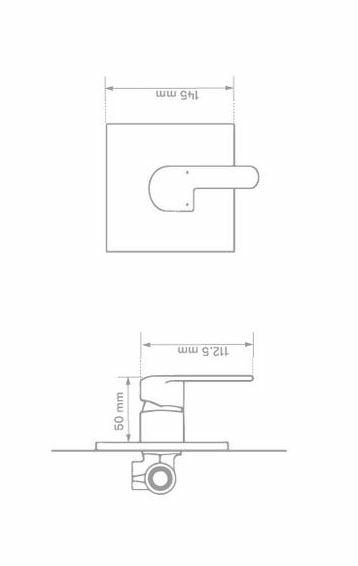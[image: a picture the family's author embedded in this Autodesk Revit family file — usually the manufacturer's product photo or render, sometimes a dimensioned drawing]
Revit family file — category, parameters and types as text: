
# Revit family: 01-1333-11 REGISTRO DUCHA ATLANTICO
name_source: partatom
category: Plumbing Fixtures
revit_build: Autodesk Revit 2018 (Build: 20170223_1515(x64)
units: mm (PartAtom-declared; Revit-internal decimal feet)

## family parameters
Cut with Voids When Loaded = No
Host = Face
OmniClass Number = 23.31.11.00
Part Type = Normal
Room Calculation Point = No
Round Connector Dimension = Use Diameter
Shared = No

## types (1)
- 01-1333-11
    Alto = 85 mm
    Ancho manija = 66 mm
    CW Connection = Yes
    Default Elevation = 0 mm  [stored 0 ft]
    Description = Registro
    Dim escudo = 60 mm
    HW Connection = Yes
    Link Ficha Tecnica = http://infotecnica.gricol.com
    Manufacturer = Gricol
    Metal Laton Cromado = Metal Laton Cromado
    Model = 01-1333-11
    Plastico - ABS Cromado = Plastico - ABS Cromado
    Product Name = REGISTRO DUCHA ATLANTICO
    Type Image = REGISTRO DUCHA ATLANTICO.JPG
    URL = https://www.gricol.com
    Vent Connection = No
    Waste Connection = No

note: [stored X ft] marks values corroborated as IEEE doubles in the binary element streams (Revit-internal decimal feet)

## geometry (parser evidence)
native form markers: Blend x4, Sweep x9
no freeform markers — native parametric forms only
